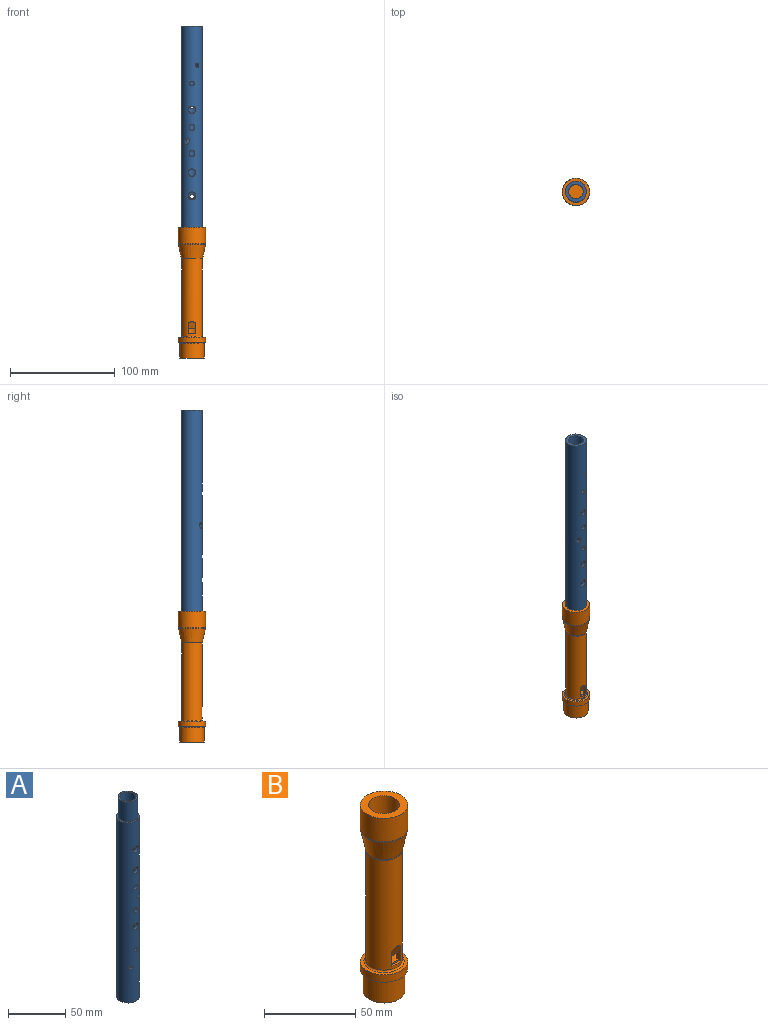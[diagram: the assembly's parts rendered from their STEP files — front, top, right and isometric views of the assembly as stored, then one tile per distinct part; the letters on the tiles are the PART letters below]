
ASSEMBLY  parts=2 mates=1
PART A: 16 faces, bbox 20x20.1x213.5 mm
  f0: cylinder r=7mm len=213.5mm, axis (0,0,-1), area 9132mm2, adj f3,f5,f6,f7,f8,f9,f10,f11
  f1: cylinder r=10mm len=192.5mm, axis (0,0,-1), area 11840.3mm2, adj f2,f3,f6,f7,f8,f9,f10,f11
  f2: plane 20x20mm, normal (0,0,1), area 87.2mm2, adj f1,f4
  f3: plane 20x20mm, normal (0,0,-1), area 160.2mm2, adj f0,f1
  f4: cylinder r=8.5mm len=21mm, axis (0,0,-1), area 1121.5mm2, adj f2,f5
  f5: plane 17x17mm, normal (0,0,1), area 73mm2, adj f0,f4
  f6: cylinder r=2.25mm len=4.5mm, axis (0,-1,0), area 43.2mm2, adj f0,f1
  f7: cylinder r=3.5mm len=7mm, axis (0,-1,0), area 69.2mm2, adj f0,f1
  f8: cylinder r=2.8mm len=5.6mm, axis (0,-1,0), area 54.4mm2, adj f0,f1
  f9: cylinder r=2.75mm len=5.5mm, axis (0,-1,0), area 53.3mm2, adj f0,f1
  f10: cylinder r=3.5mm len=7mm, axis (0,-1,0), area 69.2mm2, adj f0,f1
  f11: cylinder r=3.75mm len=7.5mm, axis (0,-1,0), area 74.7mm2, adj f0,f1
  f12: cylinder r=2mm len=4mm, axis (0,1,0), area 38.3mm2, adj f0,f1
  f13: cylinder r=2.15mm len=4.3mm, axis (0,1,0), area 41.2mm2, adj f0,f1
  f14: cylinder r=2.9mm len=6.84mm, axis (0.5,-0.87,0), area 56.4mm2, adj f0,f1
  f15: cylinder r=2mm len=5.11mm, axis (-0.5,-0.87,0), area 38.3mm2, adj f0,f1
PART B: 26 faces, bbox 28.1x28.1x125 mm
  f0: plane 17x17mm, normal (0,0,1), area 67.4mm2, adj f1,f13,f20,f21,f22
  f1: cylinder r=7mm len=81mm, axis (0,0,1), area 2968.8mm2, adj f0,f14,f20,f21
  f2: cylinder r=10mm len=73.68mm, axis (0,0,-1), area 4548.9mm2, adj f12,f19,f20,f21,f23,f24
  f3: cylinder r=11.5mm len=23mm, axis (0,0,-1), area 1011.6mm2, adj f4,f25
  f4: plane 23x23mm, normal (0,0,-1), area 399.5mm2, adj f3,f15,f16,f17,f18
  f5: cylinder r=13mm len=26mm, axis (0,0,-1), area 408.4mm2, adj f6,f7
  f6: plane 26x26mm, normal (0,0,1), area 150.8mm2, adj f5,f24
  f7: plane 26x26mm, normal (0,0,-1), area 40.1mm2, adj f5,f25
  f8: cone r=10mm half-angle=12.1deg, axis (0,0,1), area 988.6mm2, adj f11,f12
  f9: plane 26x26mm, normal (0,0,1), area 303.9mm2, adj f10,f13
  f10: cylinder r=13mm len=26mm, axis (0,0,1), area 1280.9mm2, adj f9,f11
  f11: torus R=10mm, axis (0,0,-1), area 51.6mm2, adj f8,f10
  f12: torus R=13mm, axis (0,0,1), area 39.9mm2, adj f2,f8
  f13: cylinder r=8.5mm len=21mm, axis (0,0,1), area 1121.5mm2, adj f0,f9
  f14: plane 14.5x14mm, normal (0,0,1), area 159.6mm2, adj f1,f17,f20,f21
  f15: plane 23x8mm, normal (0,1,-0.02), area 172.5mm2, adj f4,f16,f18,f19
  f16: plane 23x2mm, normal (-1,0,-0.02), area 34.5mm2, adj f4,f15,f17,f21
  f17: plane 23x8mm, normal (0,-1,-0.02), area 172.5mm2, adj f4,f14,f16,f18
  f18: plane 23x2mm, normal (1,0,-0.02), area 34.5mm2, adj f4,f15,f17,f20
  f19: plane 7x1.5mm, normal (0,0,1), area 9mm2, adj f2,f15,f20,f21
  f20: plane 81x3.31mm, normal (1,0,0), area 130.6mm2, adj f0,f1,f2,f14,f18,f19,f22,f23
  f21: plane 81x3.31mm, normal (-1,0,0), area 130.6mm2, adj f0,f1,f2,f14,f16,f19,f22,f23
  f22: plane 76x7mm, normal (0,1,0), area 532mm2, adj f0,f20,f21,f23
  f23: plane 7x6.87mm, normal (0,-0.94,-0.34), area 46.9mm2, adj f2,f20,f21,f22
  f24: torus R=11mm, axis (0,0,1), area 102.3mm2, adj f2,f6
  f25: torus R=12.5mm, axis (0,0,1), area 117.1mm2, adj f3,f7
PLACE A rot(axis=(0,1,0),180deg) t=(0,0,317.5)mm
PLACE B at identity
MATE planar A.f0 <-> B.f10  axis (0,0,-1) through (0,0,125)mm
